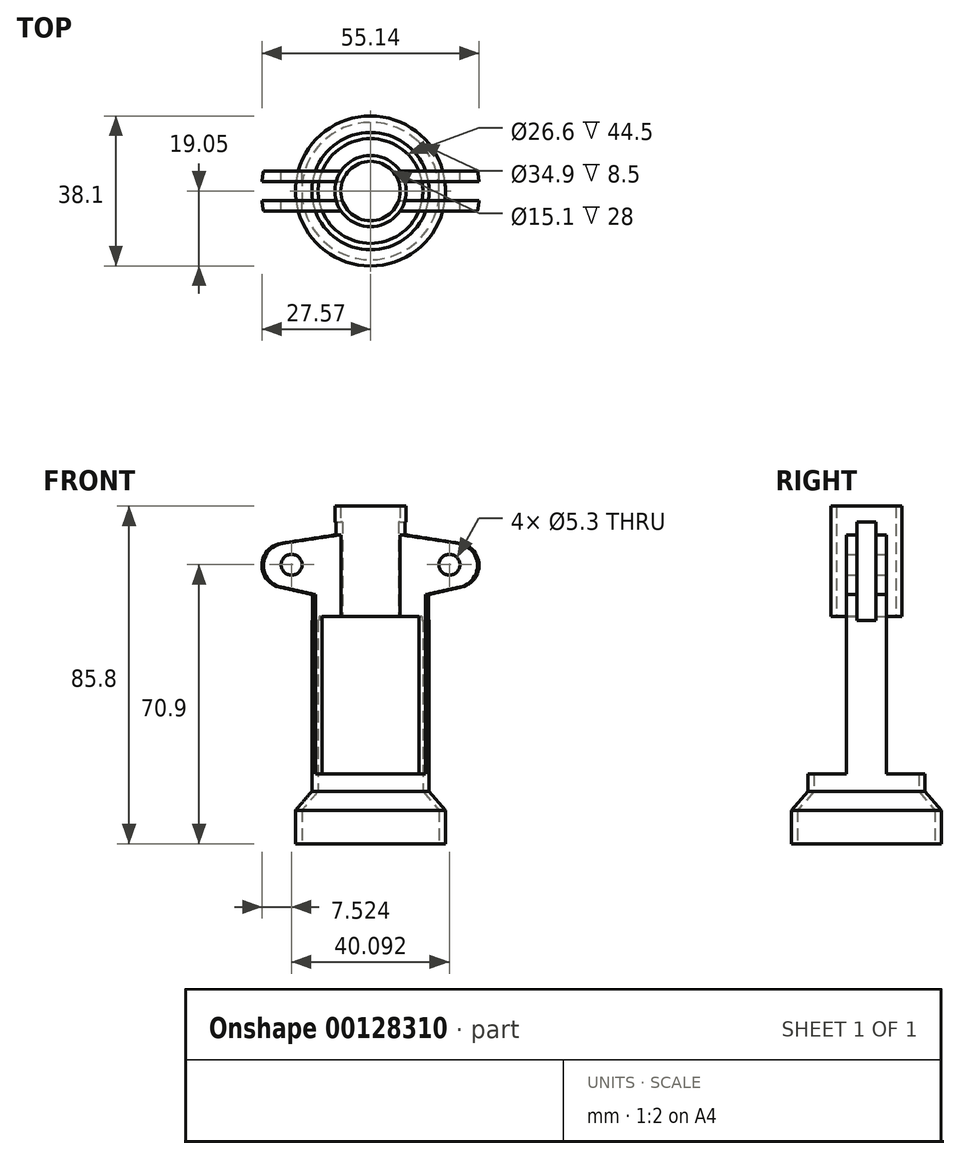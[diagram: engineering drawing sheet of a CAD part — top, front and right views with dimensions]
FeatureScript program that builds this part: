
annotation { "Feature Type Name" : "Feature", "Feature Type Description" : "" }
export const myFeature = defineFeature(function(context is Context, id is Id, definition is map)
    precondition{}
    {
        {
            var Q0;
            Q0=qCreatedBy(makeId("Front.planeOp"),FACE);
            var sketch = newSketch(context, id + "F0", { "sketchPlane" : qUnion([Q0])});
            skLineSegment(sketch, "E0", {"start": v(17.45, 0) * mm, "end": v(17.45, 8.5) * mm});
            skLineSegment(sketch, "E1", {"start": v(17.45, 0) * mm, "end": v(19.05, 0) * mm});
            skLineSegment(sketch, "E2", {"start": v(19.05, 0) * mm, "end": v(19.05, 8.5) * mm});
            skLineSegment(sketch, "E3", {"start": v(19.05, 8.5) * mm, "end": v(14.9, 13.3) * mm});
            skLineSegment(sketch, "E4", {"start": v(17.45, 8.5) * mm, "end": v(13.3, 13.3) * mm});
            skLineSegment(sketch, "E5", {"start": v(13.3, 13.3) * mm, "end": v(13.3, 57.8) * mm});
            skPoint(sketch, "E6", {"position": v(13.3, 17.8) * mm});
            skLineSegment(sketch, "E7", {"start": v(13.3, 57.8) * mm, "end": v(7.55, 57.8) * mm});
            skLineSegment(sketch, "E8", {"start": v(7.55, 57.8) * mm, "end": v(7.55, 85.8) * mm});
            skLineSegment(sketch, "E9", {"start": v(7.55, 85.8) * mm, "end": v(9.05, 85.8) * mm});
            skLineSegment(sketch, "E10", {"start": v(14.9, 13.3) * mm, "end": v(14.9, 63.3) * mm});
            skLineSegment(sketch, "E11", {"start": v(9.05, 85.8) * mm, "end": v(9.05, 78.5) * mm});
            skArc(sketch, "E12", {"start": v(23.29, 65.23) * mm, "mid": v(27.67, 70.94) * mm, "end": v(22.9, 76.32) * mm});
            skLineSegment(sketch, "E13", {"start": v(9.05, 78.5) * mm, "end": v(22.9, 76.32) * mm});
            skLineSegment(sketch, "E14", {"start": v(14.9, 63.3) * mm, "end": v(23.29, 65.23) * mm});
            skLineSegment(sketch, "E15", {"start": v(0, 0) * mm, "end": v(0, 87.13) * mm, "construction": true});
            skSolve(sketch);
        }
        {
            var Q0;
            Q0 = qSketchRegion(id + "F0", true);
            var Q1;
            Q1=sQuery(id+"F0.wireOp",EDGE,"E15");
            revolve(context, id + "F1", {"entities" : qUnion([Q0]), "axis" : qUnion([Q1]), "revolveType" : RevolveType.FULL});
        }
        {
            var Q0;
            Q0=makeQuery(id+"F1.opRevolve","SWEPT_FACE",FACE,{"disambiguationData":[OSD([sQuery(id+"F0.wireOp",EDGE,"E9")])]});
            var sketch = newSketch(context, id + "F2", { "sketchPlane" : qUnion([Q0])});
            skArc(sketch, "E16.0", {"start": v(-7.48, -5.1) * mm, "mid": v(0, -9.05) * mm, "end": v(7.48, -5.1) * mm});
            skLineSegment(sketch, "E17", {"start": v(33.85, 5.1) * mm, "end": v(33.85, 32.36) * mm});
            skLineSegment(sketch, "E18", {"start": v(33.85, 32.36) * mm, "end": v(-33.32, 32.36) * mm});
            skLineSegment(sketch, "E19", {"start": v(-33.32, 32.36) * mm, "end": v(-33.32, 5.1) * mm});
            skLineSegment(sketch, "E20", {"start": v(-33.32, 5.1) * mm, "end": v(-7.48, 5.1) * mm});
            skLineSegment(sketch, "E21", {"start": v(-31.97, 0) * mm, "end": v(36.98, 0) * mm, "construction": true});
            skLineSegment(sketch, "E22", {"start": v(7.48, 5.1) * mm, "end": v(33.85, 5.1) * mm});
            skLineSegment(sketch, "E23.MirrorCS", {"start": v(-33.32, -5.1) * mm, "end": v(-7.48, -5.1) * mm});
            skLineSegment(sketch, "E24.MirrorCS", {"start": v(-33.32, -32.36) * mm, "end": v(-33.32, -5.1) * mm});
            skLineSegment(sketch, "E25.MirrorCS", {"start": v(33.85, -32.36) * mm, "end": v(-33.32, -32.36) * mm});
            skLineSegment(sketch, "E26.MirrorCS", {"start": v(7.48, -5.1) * mm, "end": v(33.85, -5.1) * mm});
            skLineSegment(sketch, "E27.MirrorCS", {"start": v(33.85, -5.1) * mm, "end": v(33.85, -32.36) * mm});
            skArc(sketch, "E28.trimOffspring", {"start": v(7.48, 5.1) * mm, "mid": v(0, 9.05) * mm, "end": v(-7.48, 5.1) * mm});
            skSolve(sketch);
        }
        {
            var Q0;
            Q0 = qSketchRegion(id + "F2", true);
            extrude(context, id + "F3", {"entities" : qUnion([Q0]), "operationType" : NewBodyOperationType.REMOVE, "oppositeDirection" : true, "depth" : 68.1 * mm});
        }
        {
            var Q0;
            Q0=qCreatedBy(makeId("Right.planeOp"),FACE);
            var sketch = newSketch(context, id + "F4", { "sketchPlane" : qUnion([Q0])});
            skLineSegment(sketch, "E29.bottom", {"start": v(-2.43, 81.8) * mm, "end": v(2.37, 81.8) * mm});
            skLineSegment(sketch, "E29.top", {"start": v(-2.43, 56.8) * mm, "end": v(2.37, 56.8) * mm});
            skLineSegment(sketch, "E29.left", {"start": v(-2.43, 81.8) * mm, "end": v(-2.43, 56.8) * mm});
            skLineSegment(sketch, "E29.right", {"start": v(2.37, 81.8) * mm, "end": v(2.37, 56.8) * mm});
            skSolve(sketch);
        }
        {
            var Q0;
            Q0 = qSketchRegion(id + "F4", true);
            var Q1;
            Q1=makeQuery(id+"F3.boolean.opBoolean","SPLIT",FACE,{"disambiguationData":[TD([makeQuery(id+"F3.opExtrude","SWEPT_FACE",FACE,{"disambiguationData":[OSD([sQuery(id+"F2.wireOp",EDGE,"E20")])]})])],"derivedFrom":makeQuery(id+"F1.opRevolve","SWEPT_FACE",FACE,{"disambiguationData":[OSD([sQuery(id+"F0.wireOp",EDGE,"E12")])]})});
            var Q2;
            Q2=makeQuery(id+"F3.boolean.opBoolean","SPLIT",FACE,{"disambiguationData":[TD([makeQuery(id+"F3.opExtrude","SWEPT_FACE",FACE,{"disambiguationData":[OSD([sQuery(id+"F2.wireOp",EDGE,"E22")])]})])],"derivedFrom":makeQuery(id+"F1.opRevolve","SWEPT_FACE",FACE,{"disambiguationData":[OSD([sQuery(id+"F0.wireOp",EDGE,"E12")])]})});
            extrude(context, id + "F5", {"entities" : qUnion([Q0]), "operationType" : NewBodyOperationType.REMOVE, "endBound" : BoundingType.SYMMETRIC, "oppositeDirection" : true, "endBoundEntityFace" : qUnion([Q1]), "depth" : 83.62 * mm, "hasSecondDirection" : true, "secondDirectionBound" : SecondDirectionBoundingType.UP_TO_SURFACE, "secondDirectionOppositeDirection" : false, "secondDirectionBoundEntityFace" : qUnion([Q2]), "secondDirectionDepth" : 31.58 * mm});
        }
        {
            var Q0;
            Q0=makeQuery(id+"F3.boolean.opBoolean","COPY",FACE,{"derivedFrom":makeQuery(id+"F3.opExtrude","SWEPT_FACE",FACE,{"disambiguationData":[OSD([sQuery(id+"F2.wireOp",EDGE,"E22")])]})});
            var sketch = newSketch(context, id + "F6", { "sketchPlane" : qUnion([Q0])});
            skCircle(sketch, "E30", {"center": v(-20.05, 70.9) * mm, "radius": 2.65 * mm});
            skCircle(sketch, "E31.MirrorC", {"center": v(20.05, 70.9) * mm, "radius": 2.65 * mm});
            skSolve(sketch);
        }
        {
            var Q0;
            Q0 = qSketchRegion(id + "F6", true);
            extrude(context, id + "F7", {"entities" : qUnion([Q0]), "operationType" : NewBodyOperationType.REMOVE, "oppositeDirection" : true, "depth" : 25 * mm});
        }
    });
